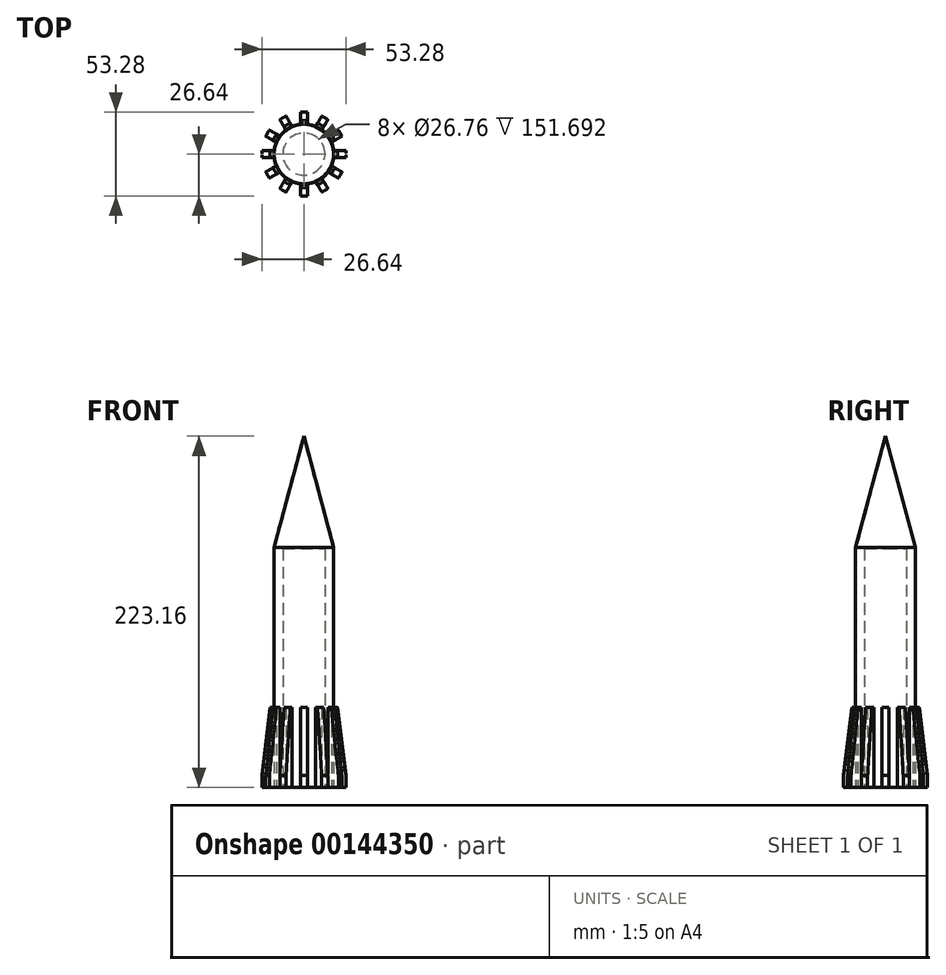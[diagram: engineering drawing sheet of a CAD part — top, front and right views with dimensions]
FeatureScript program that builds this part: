
annotation { "Feature Type Name" : "Feature", "Feature Type Description" : "" }
export const myFeature = defineFeature(function(context is Context, id is Id, definition is map)
    precondition{}
    {
        {
            var Q0;
            Q0=qCreatedBy(makeId("Top.planeOp"),FACE);
            var sketch = newSketch(context, id + "F0", { "sketchPlane" : qUnion([Q0])});
            skCircle(sketch, "E0", {"center": v(0, 0) * mm, "radius": 18.96 * mm});
            skSolve(sketch);
        }
        {
            var Q0;
            Q0=makeQuery(id+"F0.imprint","IMPRINT",FACE,{"disambiguationData":[TD([[makeQuery(id+"F0.imprint","IMPRINT",EDGE,{"derivedFrom":sQuery(id+"F0.wireOp",EDGE,"E0")}),1.0]])]});
            extrude(context, id + "F1", {"entities" : qUnion([Q0]), "depth" : 152.4 * mm});
        }
        {
            var Q0;
            Q0=makeQuery(id+"F1.opExtrude","CAP_FACE",FACE,{"disambiguationData":[OSD([sQuery(id+"F0.wireOp",EDGE,"E0")])],"isStart":false});
            var sketch = newSketch(context, id + "F2", { "sketchPlane" : qUnion([Q0])});
            skCircle(sketch, "E1.0", {"center": v(0, 0) * mm, "radius": 18.96 * mm});
            skSolve(sketch);
        }
        {
            var Q0;
            Q0 = qSketchRegion(id + "F2", true);
            extrude(context, id + "F3", {"entities" : qUnion([Q0]), "operationType" : NewBodyOperationType.ADD, "depth" : 76.2 * mm, "hasDraft" : true, "draftAngle" : 15 * degree, "draftPullDirection" : true});
        }
        {
            var Q0;
            Q0=makeQuery(id+"F1.opExtrude","CAP_FACE",FACE,{"disambiguationData":[OSD([sQuery(id+"F0.wireOp",EDGE,"E0")])],"isStart":true});
            var sketch = newSketch(context, id + "F4", { "sketchPlane" : qUnion([Q0])});
            skLineSegment(sketch, "E2.bottom", {"start": v(26.64, 2.25) * mm, "end": v(-26.64, 2.25) * mm});
            skLineSegment(sketch, "E2.top", {"start": v(26.64, -2.25) * mm, "end": v(-26.64, -2.25) * mm});
            skLineSegment(sketch, "E2.left", {"start": v(26.64, 2.25) * mm, "end": v(26.64, -2.25) * mm});
            skLineSegment(sketch, "E2.right", {"start": v(-26.64, 2.25) * mm, "end": v(-26.64, -2.25) * mm});
            skPoint(sketch, "E2.middle", {"position": v(0, 0) * mm});
            skSolve(sketch);
        }
        {
            var Q0;
            Q0 = qSketchRegion(id + "F4", true);
            extrude(context, id + "F5", {"entities" : qUnion([Q0]), "operationType" : NewBodyOperationType.ADD, "oppositeDirection" : true, "depth" : 50.8 * mm});
        }
        {
            var Q0;
            Q0=qCreatedBy(makeId("Front.planeOp"),FACE);
            var sketch = newSketch(context, id + "F6", { "sketchPlane" : qUnion([Q0])});
            skLineSegment(sketch, "E3", {"start": v(-21.01, 54.12) * mm, "end": v(-27.59, 0) * mm});
            skLineSegment(sketch, "E4", {"start": v(-27.59, 0) * mm, "end": v(-34.3, 55.48) * mm});
            skLineSegment(sketch, "E5", {"start": v(-34.3, 55.48) * mm, "end": v(-21.01, 54.12) * mm});
            skLineSegment(sketch, "E6", {"start": v(0, 0) * mm, "end": v(0, -17.35) * mm, "construction": true});
            skSolve(sketch);
        }
        {
            var Q0;
            Q0=makeQuery(id+"F6.imprint","IMPRINT",FACE,{"disambiguationData":[TD([[makeQuery(id+"F6.imprint","IMPRINT",EDGE,{"derivedFrom":sQuery(id+"F6.wireOp",EDGE,"E3")}),-1.0]])]});
            var Q1;
            Q1=sQuery(id+"F6.wireOp",EDGE,"E6");
            revolve(context, id + "F7", {"operationType" : NewBodyOperationType.REMOVE, "entities" : qUnion([Q0]), "axis" : qUnion([Q1]), "revolveType" : RevolveType.FULL, "oppositeDirection" : true});
        }
        {
            var Q0;
            Q0=qCreatedBy(makeId("Front.planeOp"),FACE);
            var sketch = newSketch(context, id + "F8", { "sketchPlane" : qUnion([Q0])});
            skLineSegment(sketch, "E7", {"start": v(0, 0) * mm, "end": v(0, -13.51) * mm, "construction": true});
            skSolve(sketch);
        }
        {
            var Q0;
            Q0=makeQuery(id+"F1.opExtrude","SWEPT_BODY",BODY,{"disambiguationData":[OSD([sQuery(id+"F0.wireOp",EDGE,"E0")])]});
            var Q1;
            Q1=sQuery(id+"F8.wireOp",EDGE,"E7");
            circularPattern(context, id + "F9", {"entities" : qUnion([Q0]), "axis" : qUnion([Q1]), "angle" : 30 * degree, "instanceCount" : 8});
        }
        {
            var Q0;
            Q0=makeQuery(id+"F5.boolean.opBoolean","MERGE",FACE,{"derivedFrom":[makeQuery(id+"F1.opExtrude","CAP_FACE",FACE,{"disambiguationData":[OSD([sQuery(id+"F0.wireOp",EDGE,"E0")])],"isStart":true}),makeQuery(id+"F5.opExtrude","CAP_FACE",FACE,{"disambiguationData":[OSD([sQuery(id+"F4.wireOp",EDGE,"E2.bottom"),sQuery(id+"F4.wireOp",EDGE,"E2.top"),sQuery(id+"F4.wireOp",EDGE,"E2.left"),sQuery(id+"F4.wireOp",EDGE,"E2.right")])],"isStart":true})]});
            var sketch = newSketch(context, id + "F10", { "sketchPlane" : qUnion([Q0])});
            skCircle(sketch, "E8", {"center": v(0, 0) * mm, "radius": 13.38 * mm});
            skSolve(sketch);
        }
        {
            var Q0;
            Q0 = qSketchRegion(id + "F10", true);
            extrude(context, id + "F11", {"entities" : qUnion([Q0]), "operationType" : NewBodyOperationType.REMOVE, "oppositeDirection" : true, "depth" : 151.7 * mm});
        }
    });
